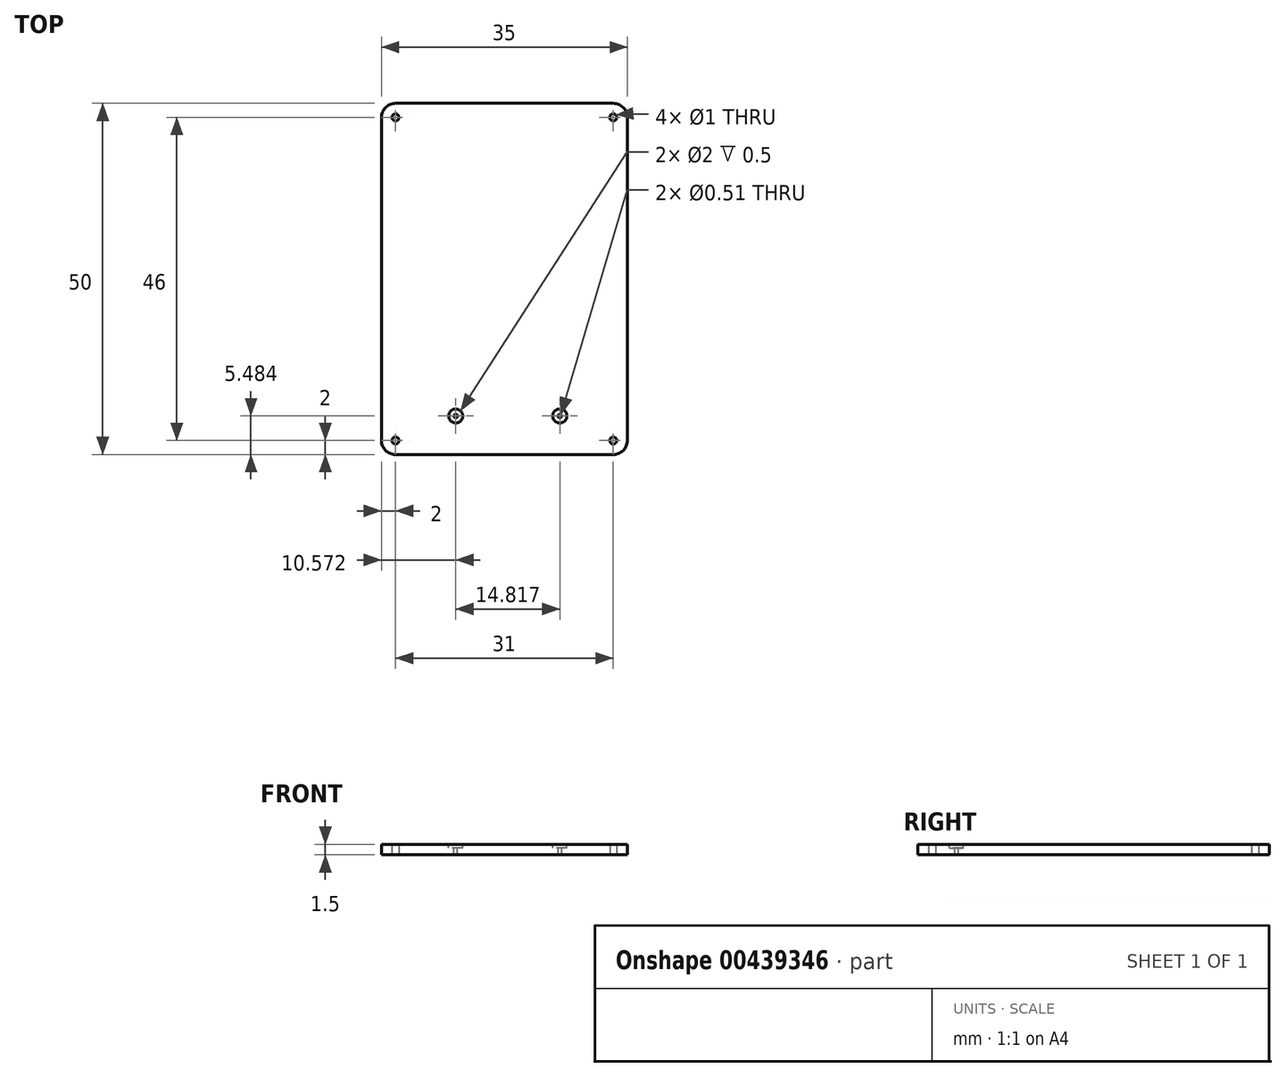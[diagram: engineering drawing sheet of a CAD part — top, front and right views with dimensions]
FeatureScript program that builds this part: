
annotation { "Feature Type Name" : "Feature", "Feature Type Description" : "" }
export const myFeature = defineFeature(function(context is Context, id is Id, definition is map)
    precondition{}
    {
        {
            var Q0;
            Q0=qCreatedBy(makeId("Top.planeOp"),FACE);
            var sketch = newSketch(context, id + "F0", { "sketchPlane" : qUnion([Q0])});
            skLineSegment(sketch, "E0.bottom", {"start": v(67, 0) * mm, "end": v(98, 0) * mm});
            skLineSegment(sketch, "E0.top", {"start": v(67, 50) * mm, "end": v(98, 50) * mm});
            skLineSegment(sketch, "E0.right", {"start": v(100, 2) * mm, "end": v(100, 48) * mm});
            skPoint(sketch, "E1.visualSharp", {"position": v(0, 50) * mm});
            skPoint(sketch, "E2.visualSharp", {"position": v(100, 50) * mm});
            skArc(sketch, "E2.filletArc", {"start": v(100, 48) * mm, "mid": v(99.41, 49.41) * mm, "end": v(98, 50) * mm});
            skPoint(sketch, "E3.visualSharp", {"position": v(100, 0) * mm});
            skArc(sketch, "E3.filletArc", {"start": v(98, 0) * mm, "mid": v(99.41, 0.59) * mm, "end": v(100, 2) * mm});
            skPoint(sketch, "E4.visualSharp", {"position": v(0, 0) * mm});
            skLineSegment(sketch, "E5", {"start": v(65, 48) * mm, "end": v(65, 2) * mm});
            skPoint(sketch, "E6.visualSharp", {"position": v(65, 50) * mm});
            skArc(sketch, "E6.filletArc", {"start": v(67, 50) * mm, "mid": v(65.59, 49.41) * mm, "end": v(65, 48) * mm});
            skPoint(sketch, "E7.visualSharp", {"position": v(65, 0) * mm});
            skArc(sketch, "E7.filletArc", {"start": v(65, 2) * mm, "mid": v(65.59, 0.59) * mm, "end": v(67, 0) * mm});
            skCircle(sketch, "E8", {"center": v(67, 2) * mm, "radius": 0.5 * mm});
            skCircle(sketch, "E9", {"center": v(67, 48) * mm, "radius": 0.5 * mm});
            skCircle(sketch, "E10", {"center": v(98, 48) * mm, "radius": 0.5 * mm});
            skCircle(sketch, "E11", {"center": v(98, 2) * mm, "radius": 0.5 * mm});
            skSolve(sketch);
        }
        {
            var Q0;
            Q0=makeQuery(id+"F0.imprint","IMPRINT",FACE,{"disambiguationData":[TD([[makeQuery(id+"F0.imprint","IMPRINT",EDGE,{"derivedFrom":sQuery(id+"F0.wireOp",EDGE,"E0.bottom")}),1.0]])]});
            extrude(context, id + "F1", {"entities" : qUnion([Q0]), "depth" : 1.5 * mm});
        }
        {
            var Q0;
            Q0=makeQuery(id+"F1.opExtrude","CAP_FACE",FACE,{"disambiguationData":[OSD([sQuery(id+"F0.wireOp",EDGE,"E0.bottom"),sQuery(id+"F0.wireOp",EDGE,"E0.top"),sQuery(id+"F0.wireOp",EDGE,"E0.left"),sQuery(id+"F0.wireOp",EDGE,"E0.right"),sQuery(id+"F0.wireOp",EDGE,"E1.filletArc"),sQuery(id+"F0.wireOp",EDGE,"E2.filletArc"),sQuery(id+"F0.wireOp",EDGE,"E3.filletArc"),sQuery(id+"F0.wireOp",EDGE,"E4.filletArc")])],"isStart":false});
            var sketch = newSketch(context, id + "F2", { "sketchPlane" : qUnion([Q0])});
            skCircle(sketch, "E12", {"center": v(90.39, 5.48) * mm, "radius": 1 * mm});
            skCircle(sketch, "E13", {"center": v(75.57, 5.48) * mm, "radius": 1 * mm});
            skSolve(sketch);
        }
        {
            var Q0;
            Q0=makeQuery(id+"F2.imprint","IMPRINT",FACE,{"disambiguationData":[TD([[makeQuery(id+"F2.imprint","IMPRINT",EDGE,{"derivedFrom":sQuery(id+"F2.wireOp",EDGE,"E12")}),1.0]])]});
            var Q1;
            Q1=makeQuery(id+"F2.imprint","IMPRINT",FACE,{"disambiguationData":[TD([[makeQuery(id+"F2.imprint","IMPRINT",EDGE,{"derivedFrom":sQuery(id+"F2.wireOp",EDGE,"E13")}),1.0]])]});
            extrude(context, id + "F3", {"entities" : qUnion([Q0, Q1]), "operationType" : NewBodyOperationType.REMOVE, "oppositeDirection" : true, "depth" : 0.5 * mm});
        }
        {
            var Q0;
            Q0=makeQuery(id+"F3.boolean.opBoolean","COPY",FACE,{"derivedFrom":makeQuery(id+"F3.opExtrude","CAP_FACE",FACE,{"disambiguationData":[OSD([sQuery(id+"F2.wireOp",EDGE,"E12")])],"isStart":false})});
            var sketch = newSketch(context, id + "F4", { "sketchPlane" : qUnion([Q0])});
            skCircle(sketch, "E14", {"center": v(90.39, 5.48) * mm, "radius": 0.26 * mm});
            skSolve(sketch);
        }
        {
            var Q0;
            Q0 = qSketchRegion(id + "F4", true);
            extrude(context, id + "F5", {"entities" : qUnion([Q0]), "operationType" : NewBodyOperationType.REMOVE, "oppositeDirection" : true, "depth" : 1 * mm});
        }
        {
            var Q0;
            Q0=makeQuery(id+"F3.boolean.opBoolean","COPY",FACE,{"derivedFrom":makeQuery(id+"F3.opExtrude","CAP_FACE",FACE,{"disambiguationData":[OSD([sQuery(id+"F2.wireOp",EDGE,"E13")])],"isStart":false})});
            var sketch = newSketch(context, id + "F6", { "sketchPlane" : qUnion([Q0])});
            skCircle(sketch, "E15", {"center": v(75.57, 5.48) * mm, "radius": 0.26 * mm});
            skSolve(sketch);
        }
        {
            var Q0;
            Q0 = qSketchRegion(id + "F6", true);
            extrude(context, id + "F7", {"entities" : qUnion([Q0]), "operationType" : NewBodyOperationType.REMOVE, "oppositeDirection" : true, "depth" : 1 * mm});
        }
    });
